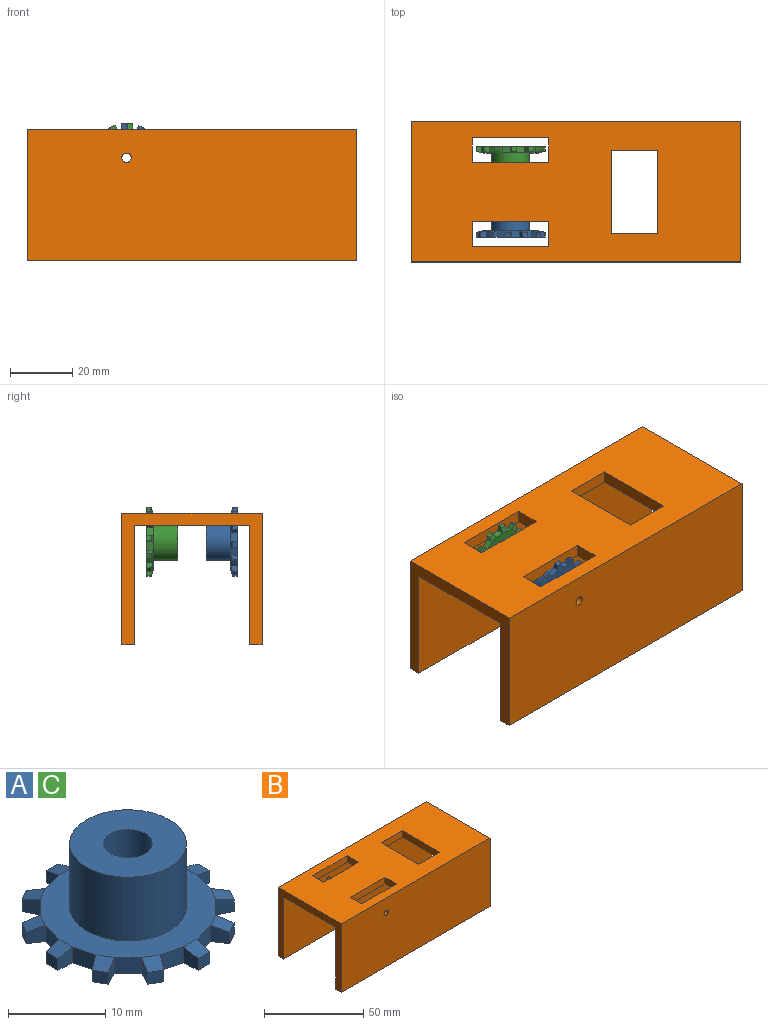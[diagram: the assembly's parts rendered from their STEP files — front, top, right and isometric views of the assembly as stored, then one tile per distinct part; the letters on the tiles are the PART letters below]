
ASSEMBLY  parts=3 mates=2
PART A: 65 faces, bbox 22.1x22.1x10 mm
  f0: plane 2.67x2mm, normal (0.26,0.97,0), area 5.5mm2, adj f1,f2,f5,f8
  f1: plane 18.09x18.09mm, normal (0,0,1), area 143.8mm2, adj f0,f4,f7,f9,f12,f14,f17,f19
  f2: plane 22.09x22.09mm, normal (0,0,-1), area 281.5mm2, adj f0,f3,f5,f6,f7,f8,f10,f11
  f3: plane 2x2mm, normal (-1,0.07,0), area 3.5mm2, adj f2,f4,f6,f57
  f4: plane 2x1.98mm, normal (0,0.26,0.97), area 3.8mm2, adj f1,f3,f5,f6
  f5: plane 2x2mm, normal (1,0.07,0), area 3.5mm2, adj f0,f2,f4,f6
  f6: plane 1.7x1.46mm, normal (0,1,0), area 2.5mm2, adj f2,f3,f4,f5
  f7: plane 2x1.96mm, normal (0.71,0.71,0), area 5.5mm2, adj f1,f2,f10,f13
  f8: plane 2x1.66mm, normal (-0.83,0.56,0), area 3.5mm2, adj f0,f2,f9,f11
  f9: plane 2.65x2.59mm, normal (0.13,0.22,0.97), area 3.8mm2, adj f1,f8,f10,f11
  f10: plane 2x1.8mm, normal (0.9,-0.44,0), area 3.5mm2, adj f2,f7,f9,f11
  f11: plane 1.47x1.46mm, normal (0.5,0.87,0), area 2.5mm2, adj f2,f8,f9,f10
  f12: plane 2.67x2mm, normal (0.97,0.26,0), area 5.5mm2, adj f1,f2,f15,f18
  f13: plane 2x1.8mm, normal (-0.44,0.9,0), area 3.5mm2, adj f2,f7,f14,f16
  f14: plane 2.65x2.59mm, normal (0.22,0.13,0.97), area 3.8mm2, adj f1,f13,f15,f16
  f15: plane 2x1.66mm, normal (0.56,-0.83,0), area 3.5mm2, adj f2,f12,f14,f16
  f16: plane 1.47x1.46mm, normal (0.87,0.5,0), area 2.5mm2, adj f2,f13,f14,f15
  f17: plane 2.67x2mm, normal (0.97,-0.26,0), area 5.5mm2, adj f1,f2,f20,f23
  f18: plane 2x2mm, normal (0.07,1,0), area 3.5mm2, adj f2,f12,f19,f21
  f19: plane 2x1.98mm, normal (0.26,0,0.97), area 3.8mm2, adj f1,f18,f20,f21
  f20: plane 2x2mm, normal (0.07,-1,0), area 3.5mm2, adj f2,f17,f19,f21
  f21: plane 1.7x1.46mm, normal (1,0,0), area 2.5mm2, adj f2,f18,f19,f20
  f22: plane 2x1.96mm, normal (0.71,-0.71,0), area 5.5mm2, adj f1,f2,f25,f28
  f23: plane 2x1.66mm, normal (0.56,0.83,0), area 3.5mm2, adj f2,f17,f24,f26
  f24: plane 2.65x2.59mm, normal (0.22,-0.13,0.97), area 3.8mm2, adj f1,f23,f25,f26
  f25: plane 2x1.8mm, normal (-0.44,-0.9,0), area 3.5mm2, adj f2,f22,f24,f26
  f26: plane 1.47x1.46mm, normal (0.87,-0.5,0), area 2.5mm2, adj f2,f23,f24,f25
  f27: plane 2.67x2mm, normal (0.26,-0.97,0), area 5.5mm2, adj f1,f2,f30,f33
  f28: plane 2x1.8mm, normal (0.9,0.44,0), area 3.5mm2, adj f2,f22,f29,f31
  f29: plane 2.65x2.59mm, normal (0.13,-0.22,0.97), area 3.8mm2, adj f1,f28,f30,f31
  f30: plane 2x1.66mm, normal (-0.83,-0.56,0), area 3.5mm2, adj f2,f27,f29,f31
  f31: plane 1.47x1.46mm, normal (0.5,-0.87,0), area 2.5mm2, adj f2,f28,f29,f30
  f32: plane 2.67x2mm, normal (-0.26,-0.97,0), area 5.5mm2, adj f1,f2,f35,f38
  f33: plane 2x2mm, normal (1,-0.07,0), area 3.5mm2, adj f2,f27,f34,f36
  f34: plane 2x1.98mm, normal (0,-0.26,0.97), area 3.8mm2, adj f1,f33,f35,f36
  f35: plane 2x2mm, normal (-1,-0.07,0), area 3.5mm2, adj f2,f32,f34,f36
  f36: plane 1.7x1.46mm, normal (0,-1,0), area 2.5mm2, adj f2,f33,f34,f35
  f37: plane 2x1.96mm, normal (-0.71,-0.71,0), area 5.5mm2, adj f1,f2,f40,f43
  f38: plane 2x1.66mm, normal (0.83,-0.56,0), area 3.5mm2, adj f2,f32,f39,f41
  f39: plane 2.65x2.59mm, normal (-0.13,-0.22,0.97), area 3.8mm2, adj f1,f38,f40,f41
  f40: plane 2x1.8mm, normal (-0.9,0.44,0), area 3.5mm2, adj f2,f37,f39,f41
  f41: plane 1.47x1.46mm, normal (-0.5,-0.87,0), area 2.5mm2, adj f2,f38,f39,f40
  f42: plane 2.67x2mm, normal (-0.97,-0.26,0), area 5.5mm2, adj f1,f2,f45,f48
  f43: plane 2x1.8mm, normal (0.44,-0.9,0), area 3.5mm2, adj f2,f37,f44,f46
  f44: plane 2.65x2.59mm, normal (-0.22,-0.13,0.97), area 3.8mm2, adj f1,f43,f45,f46
  f45: plane 2x1.66mm, normal (-0.56,0.83,0), area 3.5mm2, adj f2,f42,f44,f46
  f46: plane 1.47x1.46mm, normal (-0.87,-0.5,0), area 2.5mm2, adj f2,f43,f44,f45
  f47: plane 2.67x2mm, normal (-0.97,0.26,0), area 5.5mm2, adj f1,f2,f50,f53
  f48: plane 2x2mm, normal (-0.07,-1,0), area 3.5mm2, adj f2,f42,f49,f51
  f49: plane 2x1.98mm, normal (-0.26,0,0.97), area 3.8mm2, adj f1,f48,f50,f51
  f50: plane 2x2mm, normal (-0.07,1,0), area 3.5mm2, adj f2,f47,f49,f51
  f51: plane 1.7x1.46mm, normal (-1,0,0), area 2.5mm2, adj f2,f48,f49,f50
  f52: plane 2x1.96mm, normal (-0.71,0.71,0), area 5.5mm2, adj f1,f2,f55,f58
  f53: plane 2x1.66mm, normal (-0.56,-0.83,0), area 3.5mm2, adj f2,f47,f54,f56
  f54: plane 2.65x2.59mm, normal (-0.22,0.13,0.97), area 3.8mm2, adj f1,f53,f55,f56
  f55: plane 2x1.8mm, normal (0.44,0.9,0), area 3.5mm2, adj f2,f52,f54,f56
  f56: plane 1.47x1.46mm, normal (-0.87,0.5,0), area 2.5mm2, adj f2,f53,f54,f55
  f57: plane 2.67x2mm, normal (-0.26,0.97,0), area 5.5mm2, adj f1,f2,f3,f60
  f58: plane 2x1.8mm, normal (-0.9,-0.44,0), area 3.5mm2, adj f2,f52,f59,f61
  f59: plane 2.65x2.59mm, normal (-0.13,0.22,0.97), area 3.8mm2, adj f1,f58,f60,f61
  f60: plane 2x1.66mm, normal (0.83,0.56,0), area 3.5mm2, adj f2,f57,f59,f61
  f61: plane 1.47x1.46mm, normal (-0.5,0.87,0), area 2.5mm2, adj f2,f58,f59,f60
  f62: cylinder r=2.5mm len=10mm, axis (0,0,-1), area 157.1mm2, adj f2,f64
  f63: cylinder r=6mm len=12mm, axis (0,0,-1), area 301.6mm2, adj f1,f64
  f64: plane 12x12mm, normal (0,0,1), area 93.5mm2, adj f62,f63
PART B: 24 faces, bbox 105.7x45x42.2 mm
  f0: plane 105.74x37mm, normal (0,0,-1), area 3116.2mm2, adj f1,f2,f3,f4,f5,f6,f7,f9
  f1: plane 8x4mm, normal (1,0,0), area 32mm2, adj f0,f2,f10,f11
  f2: plane 24.63x4mm, normal (0,-1,0), area 98.5mm2, adj f0,f1,f3,f11
  f3: plane 8x4mm, normal (-1,0,0), area 32mm2, adj f0,f2,f10,f11
  f4: plane 26.79x4mm, normal (-1,0,0), area 107.2mm2, adj f0,f5,f11,f18
  f5: plane 15x4mm, normal (0,1,0), area 60mm2, adj f0,f4,f6,f11
  f6: plane 26.79x4mm, normal (1,0,0), area 107.2mm2, adj f0,f5,f11,f18
  f7: plane 45x42.16mm, normal (-1,0,0), area 485.3mm2, adj f0,f8,f11,f13,f14,f19,f22,f23
  f8: plane 105.74x42.16mm, normal (0,-1,0), area 4450.7mm2, adj f7,f9,f11,f12,f13
  f9: plane 45x42.16mm, normal (1,0,0), area 485.3mm2, adj f0,f8,f11,f13,f14,f19,f22,f23
  f10: plane 24.63x4mm, normal (0,1,0), area 98.5mm2, adj f0,f1,f3,f11
  f11: plane 105.74x45mm, normal (0,0,1), area 3962.1mm2, adj f1,f2,f3,f4,f5,f6,f7,f8
  f12: cylinder r=1.5mm len=4mm, axis (0,-1,0), area 37.7mm2, adj f8,f14
  f13: plane 105.74x4mm, normal (0,0,-1), area 422.9mm2, adj f7,f8,f9,f14
  f14: plane 105.74x38.16mm, normal (0,1,0), area 4027.8mm2, adj f0,f7,f9,f12,f13
  f15: plane 8x4mm, normal (1,0,0), area 32mm2, adj f0,f11,f16,f20
  f16: plane 24.63x4mm, normal (0,1,0), area 98.5mm2, adj f0,f11,f15,f17
  f17: plane 8x4mm, normal (-1,0,0), area 32mm2, adj f0,f11,f16,f20
  f18: plane 15x4mm, normal (0,-1,0), area 60mm2, adj f0,f4,f6,f11
  f19: plane 105.74x42.16mm, normal (0,1,0), area 4450.7mm2, adj f7,f9,f11,f21,f22
  f20: plane 24.63x4mm, normal (0,-1,0), area 98.5mm2, adj f0,f11,f15,f17
  f21: cylinder r=1.5mm len=4mm, axis (0,1,0), area 37.7mm2, adj f19,f23
  f22: plane 105.74x4mm, normal (0,0,-1), area 422.9mm2, adj f7,f9,f19,f23
  f23: plane 105.74x38.16mm, normal (0,-1,0), area 4027.8mm2, adj f0,f7,f9,f21,f22
PART C: same geometry as A
PLACE A rot(axis=(-0.22,0.69,0.69),155.7deg) t=(-96.59,8,67.61)mm
PLACE B t=(-74.86,37.34,38.16)mm
PLACE C rot(axis=(0.73,0.48,-0.48),107.4deg) t=(-36.41,37,50.58)mm
MATE revolute A.f62 <-> B.f12  axis (0,1,0) through (-73.87,10,33.06)mm
MATE revolute C.f62 <-> B.f12  axis (0,-1,0) through (-73.87,35,33.06)mm
